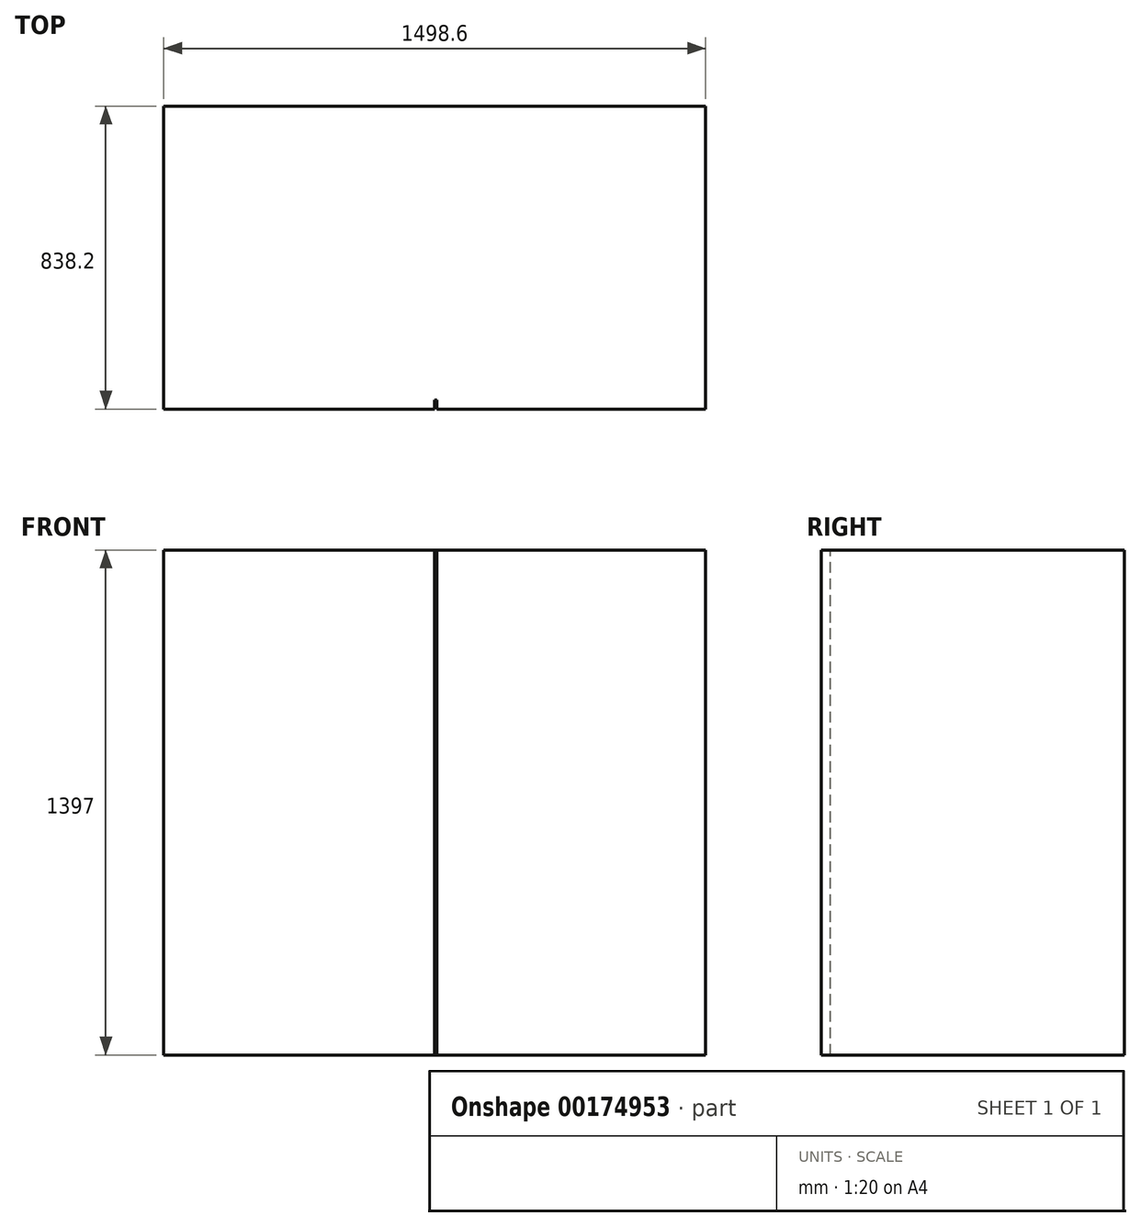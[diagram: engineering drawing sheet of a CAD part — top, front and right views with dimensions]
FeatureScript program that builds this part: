
annotation { "Feature Type Name" : "Feature", "Feature Type Description" : "" }
export const myFeature = defineFeature(function(context is Context, id is Id, definition is map)
    precondition{}
    {
        {
            var Q0;
            Q0=qCreatedBy(makeId("Top.planeOp"),FACE);
            var sketch = newSketch(context, id + "F0", { "sketchPlane" : qUnion([Q0])});
            skLineSegment(sketch, "E0.bottom", {"start": v(749.3, -419.1) * mm, "end": v(-749.3, -419.1) * mm});
            skLineSegment(sketch, "E0.top", {"start": v(749.3, 419.1) * mm, "end": v(-749.3, 419.1) * mm});
            skLineSegment(sketch, "E0.left", {"start": v(749.3, -419.1) * mm, "end": v(749.3, 419.1) * mm});
            skLineSegment(sketch, "E0.right", {"start": v(-749.3, -419.1) * mm, "end": v(-749.3, 419.1) * mm});
            skPoint(sketch, "E0.middle", {"position": v(0, 0) * mm});
            skLineSegment(sketch, "E1.bottom", {"start": v(-2.54, -419.1) * mm, "end": v(2.54, -419.1) * mm});
            skLineSegment(sketch, "E1.top", {"start": v(-2.54, 419.1) * mm, "end": v(2.54, 419.1) * mm});
            skLineSegment(sketch, "E1.left", {"start": v(-2.54, -419.1) * mm, "end": v(-2.54, 419.1) * mm});
            skLineSegment(sketch, "E1.right", {"start": v(2.54, -419.1) * mm, "end": v(2.54, 419.1) * mm});
            skSolve(sketch);
        }
        {
            var Q0;
            {var subQ0=sQuery(id+"F0.wireOp",EDGE,"E0.left");Q0=makeQuery(id+"F0.imprint","IMPRINT",FACE,{"disambiguationData":[TD([[makeQuery(id+"F0.imprint","IMPRINT",EDGE,{"derivedFrom":subQ0}),1.0]])]});}
            var Q1;
            {var subQ2=sQuery(id+"F0.wireOp",EDGE,"E0.right");Q1=makeQuery(id+"F0.imprint","IMPRINT",FACE,{"disambiguationData":[TD([[makeQuery(id+"F0.imprint","IMPRINT",EDGE,{"derivedFrom":subQ2}),-1.0]])]});}
            var Q2;
            {var subQ0=sQuery(id+"F0.wireOp",EDGE,"E1.left");Q2=makeQuery(id+"F0.imprint","IMPRINT",FACE,{"disambiguationData":[TD([[makeQuery(id+"F0.imprint","IMPRINT",EDGE,{"derivedFrom":subQ0}),-1.0]])]});}
            extrude(context, id + "F1", {"entities" : qUnion([Q0, Q1, Q2]), "depth" : 1397 * mm});
        }
        {
            var Q0;
            Q0=makeQuery(id+"F1.opExtrude","SWEPT_FACE",FACE,{"disambiguationData":[OSD([sQuery(id+"F0.wireOp",EDGE,"E0.bottom")])]});
            var sketch = newSketch(context, id + "F2", { "sketchPlane" : qUnion([Q0])});
            skLineSegment(sketch, "E2.bottom", {"start": v(0, 0) * mm, "end": v(6.35, 0) * mm});
            skLineSegment(sketch, "E2.top", {"start": v(0, 1397) * mm, "end": v(6.35, 1397) * mm});
            skLineSegment(sketch, "E2.left", {"start": v(0, 0) * mm, "end": v(0, 1397) * mm});
            skLineSegment(sketch, "E2.right", {"start": v(6.35, 0) * mm, "end": v(6.35, 1397) * mm});
            skSolve(sketch);
        }
        {
            var Q0;
            Q0=makeQuery(id+"F2.imprint","IMPRINT",FACE,{"disambiguationData":[TD([[makeQuery(id+"F2.imprint","IMPRINT",EDGE,{"derivedFrom":sQuery(id+"F2.wireOp",EDGE,"E2.bottom")}),-1.0]])]});
            extrude(context, id + "F3", {"entities" : qUnion([Q0]), "operationType" : NewBodyOperationType.REMOVE, "oppositeDirection" : true, "depth" : 25.4 * mm});
        }
    });
